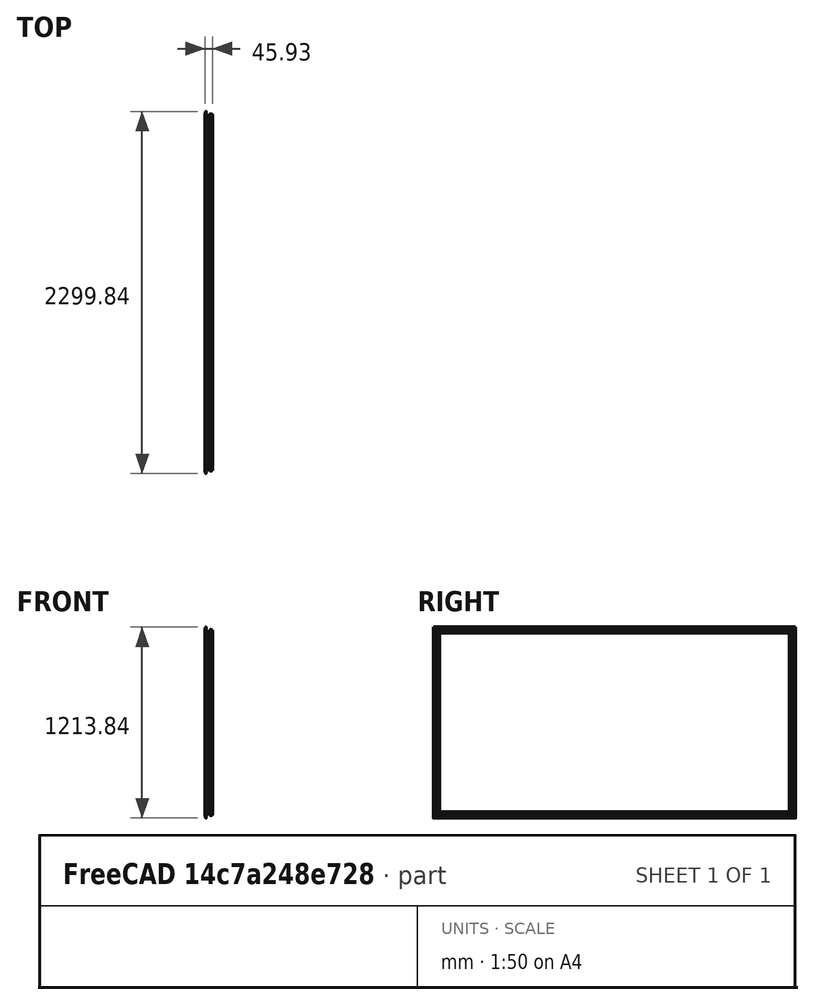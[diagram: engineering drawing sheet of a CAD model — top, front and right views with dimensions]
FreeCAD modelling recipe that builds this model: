
FCSTD DOCUMENT  (FreeCAD 0.18R4 (GitTag))
Label: door-sealing-2
License: All rights reserved
LicenseURL: http://en.wikipedia.org/wiki/All_rights_reserved
objects: Sketcher::SketchObject×2, PartDesign::Body×2, PartDesign::AdditivePipe×1, PartDesign::Mirrored×1, PartDesign::FeatureBase×1, PartDesign::Boolean×1
note: 9 computed .brp shape members not serialized (recipe doc carries the construction recipe); baked Part::Feature solids carry a one-line shape summary decoded from their .brp

FEATURE [Sketcher::SketchObject] Sketch
  MapMode = 5
  Support = -> [XY_Plane]
  sketch-geometry (11):
    g0: LineSegment StartX=0 StartY=0 StartZ=0 EndX=0 EndY=12.321 EndZ=0
    g1: ArcOfCircle CenterX=-10 CenterY=-4.99951 CenterZ=0 NormalX=0 NormalY=0 NormalZ=1 AngleXU=0 Radius=20 StartAngle=1.0472 EndAngle=2.0944
    g2: LineSegment StartX=-20 StartY=12.321 StartZ=0 EndX=-20 EndY=5 EndZ=0
    g3: LineSegment StartX=-20 StartY=5 StartZ=0 EndX=-35 EndY=5 EndZ=0
    g4: LineSegment StartX=-39.9228 StartY=9.92283 StartZ=0 EndX=-39.9228 EndY=29.9228 EndZ=0
    g5: ArcOfCircle CenterX=34.6876 CenterY=12.2716 CenterZ=0 NormalX=0 NormalY=0 NormalZ=1 AngleXU=0 Radius=80.6175 StartAngle=2.91514 EndAngle=3.36305
    g6: LineSegment StartX=-35 StartY=0 StartZ=0 EndX=0 EndY=0 EndZ=0
    g7: ArcOfCircle CenterX=-41.9228 CenterY=29.9228 CenterZ=0 NormalX=0 NormalY=0 NormalZ=1 AngleXU=0 Radius=2 StartAngle=6.28319 EndAngle=9.19833
    g8: ArcOfCircle CenterX=-42.01 CenterY=-4.997 CenterZ=0 NormalX=0 NormalY=0 NormalZ=1 AngleXU=0 Radius=2 StartAngle=3.36305 EndAngle=6.28133
    g9: ArcOfCircle CenterX=-35 CenterY=-5.01 CenterZ=0 NormalX=0 NormalY=0 NormalZ=1 AngleXU=0 Radius=5.01 StartAngle=1.5708 EndAngle=3.13974
    g10: ArcOfCircle CenterX=-35 CenterY=9.92283 CenterZ=0 NormalX=0 NormalY=0 NormalZ=1 AngleXU=0 Radius=4.92283 StartAngle=3.14159 EndAngle=4.71239
  constraints (35):
    c: Coincident(g0,g-1)
    c: PointOnObject(g0,g-2)
    c: Coincident(g1,g0)
    c: Coincident(g2,g1)
    c: Vertical(g2)
    c: Coincident(g3,g2)
    c: Horizontal(g3)
    c: Vertical(g4)
    c: Coincident(g6,g0)
    c: Horizontal(g6)
    c: Coincident(g7,g4)
    c: Coincident(g7,g5)
    c: Coincident(g8,g5)
    c: Tangent(g6,g9) = 1.5708
    c: Tangent(g3,g10) = 1.5708
    c: Tangent(g4,g10) = 1.5708
    c: Tangent(g7,g4)
    c: Tangent(g5,g7)
    c: Tangent(g8,g5)
    c: Radius(g1) = 20
    c: DistanceX(g2,g0) = 20
    c: DistanceY(g0,g0) = 12.321
    c: DistanceY(g6,g3) = 5
    c: DistanceX(g3,g3) = 15
    c: DistanceX(g6,g6) = 35
    c: DistanceY(g8,g6) = 4.997
    c: Radius(g8) = 2
    c: Radius(g7) = 2
    c: DistanceY(g4,g4) = 20
    c: Coincident(g8,g9)
    c: Tangent(g9,g8)
    c: Distance(g0,g5) = 44.296
    c: DistanceY(g0,g1) = 12.321
    c: Distance(g0,g5) = 53.359
    c: Radius(g9) = 5.01
FEATURE [Sketcher::SketchObject] Sketch001
  MapMode = 5
  Placement = pos=(0,0,0) rot=(0.57735,0.57735,0.57735;2.0944rad)
  Support = -> [YZ_Plane]
  sketch-geometry (4):
    g0: LineSegment StartX=0 StartY=-575 StartZ=0 EndX=0 EndY=0 EndZ=0
    g1: LineSegment StartX=0 StartY=-575 StartZ=0 EndX=-1118 EndY=-575 EndZ=0
    g2: LineSegment StartX=-1118 StartY=-575 StartZ=0 EndX=-1118 EndY=0 EndZ=0
    g3: LineSegment StartX=0 StartY=0 StartZ=0 EndX=-1118 EndY=0 EndZ=0
  constraints (11):
    c: Vertical(g0)
    c: DistanceY(g0,g0) = 575
    c: Coincident(g0,g-1)
    c: Coincident(g1,g0)
    c: Horizontal(g1)
    c: Coincident(g2,g1)
    c: PointOnObject(g2,g-1)
    c: Vertical(g2)
    c: DistanceX(g1,g1) = 1118
    c: Coincident(g3,g0)
    c: Coincident(g3,g2)
FEATURE [PartDesign::AdditivePipe] AdditivePipe
  AuxilleryCurvelinear = true
  AuxillerySpineTangent = false
  Binormal = (0,0,0)
  Mode = 0
  Profile = -> Sketch
  Refine = true
  Spine = -> Sketch001 [Edge1,Edge4]
  SpineTangent = false
  Transformation = 0
  Transition = 1
FEATURE [PartDesign::Mirrored] Mirrored
  BaseFeature = -> AdditivePipe
  MirrorPlane = -> AdditivePipe [Face14]
  Originals = -> [AdditivePipe]
  Refine = true
FEATURE [PartDesign::Body] Body
  Group = -> [Sketch,Sketch001,AdditivePipe,Mirrored,Boolean]
  Origin = -> Origin
  Tip = -> Boolean
FEATURE [PartDesign::Body] Body001
  Group = -> [Clone]
  Origin = -> Origin001
  Placement = pos=(-2.738e-13,-2236,0) rot=(-1,0,0;3.14159rad)
  Tip = -> Clone
FEATURE [PartDesign::FeatureBase] Clone
  BaseFeature = -> Body
FEATURE [PartDesign::Boolean] Boolean
  BaseFeature = -> Mirrored
  Group = -> [Body001]
  Refine = true
  Type = 0
